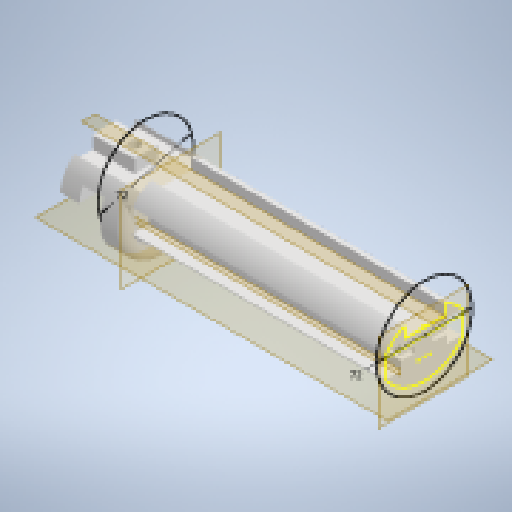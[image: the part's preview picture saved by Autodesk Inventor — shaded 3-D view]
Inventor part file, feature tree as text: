
AUTODESK INVENTOR PART (.ipt)
format: ipt  version: 2023 (Build 270158030, 158C)  size: 491,520 bytes
history: native  units: in
note: dims shown in document units (in); Inventor stores cm internally (conversion verified against a paired STEP export)
features: sketch x9, extrude x6, fillet x6, plane x5, other x2, hole x1, projected_geometry x1
ambient origin geometry x8: Origin, YZ Plane, XZ Plane, XY Plane, X Axis, Y Axis, Z Axis, Center Point
bodies: Solid1 (feature_tree)
feature tree (30):
  extrude  "Extrusion1"  Depth=2.3228in
  plane  "Work Plane1"
  extrude  "Extrusion2"  Depth=1.7126in
  other  "Full Round Fillet1"
  other  "Full Round Fillet2"
  hole  "Hole1"  [1 undecoded]
  plane  "Work Plane2"
  extrude  "Extrusion3"  Depth=1.1614in
  plane  "Work Plane3"
  sketch  "Sketch7"  dims[d11=0.0in d14=0.1969in d15=7.4803in d16=0.0in d17=0.315in d18=1.1995in d19=0.315in]
  fillet  "Fillet5"  Radius=2.6772in
  extrude  "Extrusion5"  Depth=0.1969in
  fillet  "Fillet10"  Radius=7.4803in
  fillet  "Fillet11"  Radius=0.315in
  fillet  "Fillet12"  Radius=1.1995in
  fillet  "Fillet13"  Radius=0.315in
  fillet  "Fillet14"  [1 undecoded]
  sketch  "Sketch12"  dims[d28=0.5315in d29=1.2402in]
  plane  "Work Plane4"
  extrude  "Extrusion6"  Depth=1.2402in
  plane  "Work Plane5"
  extrude  "Extrusion7"  Depth=0.5315in
  sketch  "Sketch1"  dims[d0=1.9685in d1=2.3228in]
  sketch  "Sketch2"  dims[d2=0.7677in d3=1.7126in]
  sketch  "Sketch3"  dims[d5=0.3937in d6=0.5709in]
  sketch  "Sketch4"  dims[d7=0.9843in d8=1.1614in d9=2.6772in d10=0.0in]
  projected_geometry  "Projected Loop2"
  sketch  "Sketch11"  dims[d20=0.315in d21=0.2362in d22=0.1575in d23=0.0787in d24=90.0deg d25=0.315in d26=0.8108in d27=0.0in]
  sketch  "Sketch13"  dims[d30=0.7087in d31=0.5315in]
  sketch  "Sketch14"  dims[d32=1.9685in d33=0.2953in d34=7.4803in d35=1.1811in d36=7.4803in d37=0.2953in d38=0.3543in d43=0.5512in d44=0.3937in d45=0.0in d46=0.0in d65=0.6299in d67=2.2835in d69=1.7717in d70=0.2953in d71=1.1811in d72=1.1811in d85=7.4803in d86=0.0in d93=0.3937in d94=0.1378in d95=0.3937in d100=0.3937in d101=0.3937in d104=0.4724in d105=0.2644in d106=0.2644in d107=0.4724in d108=0.4724in d110=0.4724in d111=0.2644in d112=0.2644in d113=0.1378in d114=0.0787in d115=0.0787in d116=0.0787in d117=0.0787in d118=0.0787in d120=2.8346in d121=2.8346in d122=0.7874in d123=0.2362in d124=0.7874in d125=0.2362in d126=0.7874in d127=0.0in d128=0.0in d129=0.315in d130=0.7874in d131=0.9843in d132=0.0in d133=0.315in d134=0.7874in d135=0.315in d136=0.7874in d137=0.2362in d138=0.7874in d139=0.2362in d140=0.7874in d143=0.315in d144=0.7874in d119=0.0in]
note: 2 required parameter values undecoded (feature->parameter linkage not recoverable at this tier; creation-order binding heuristic only, values carry confidence <= 0.55)
